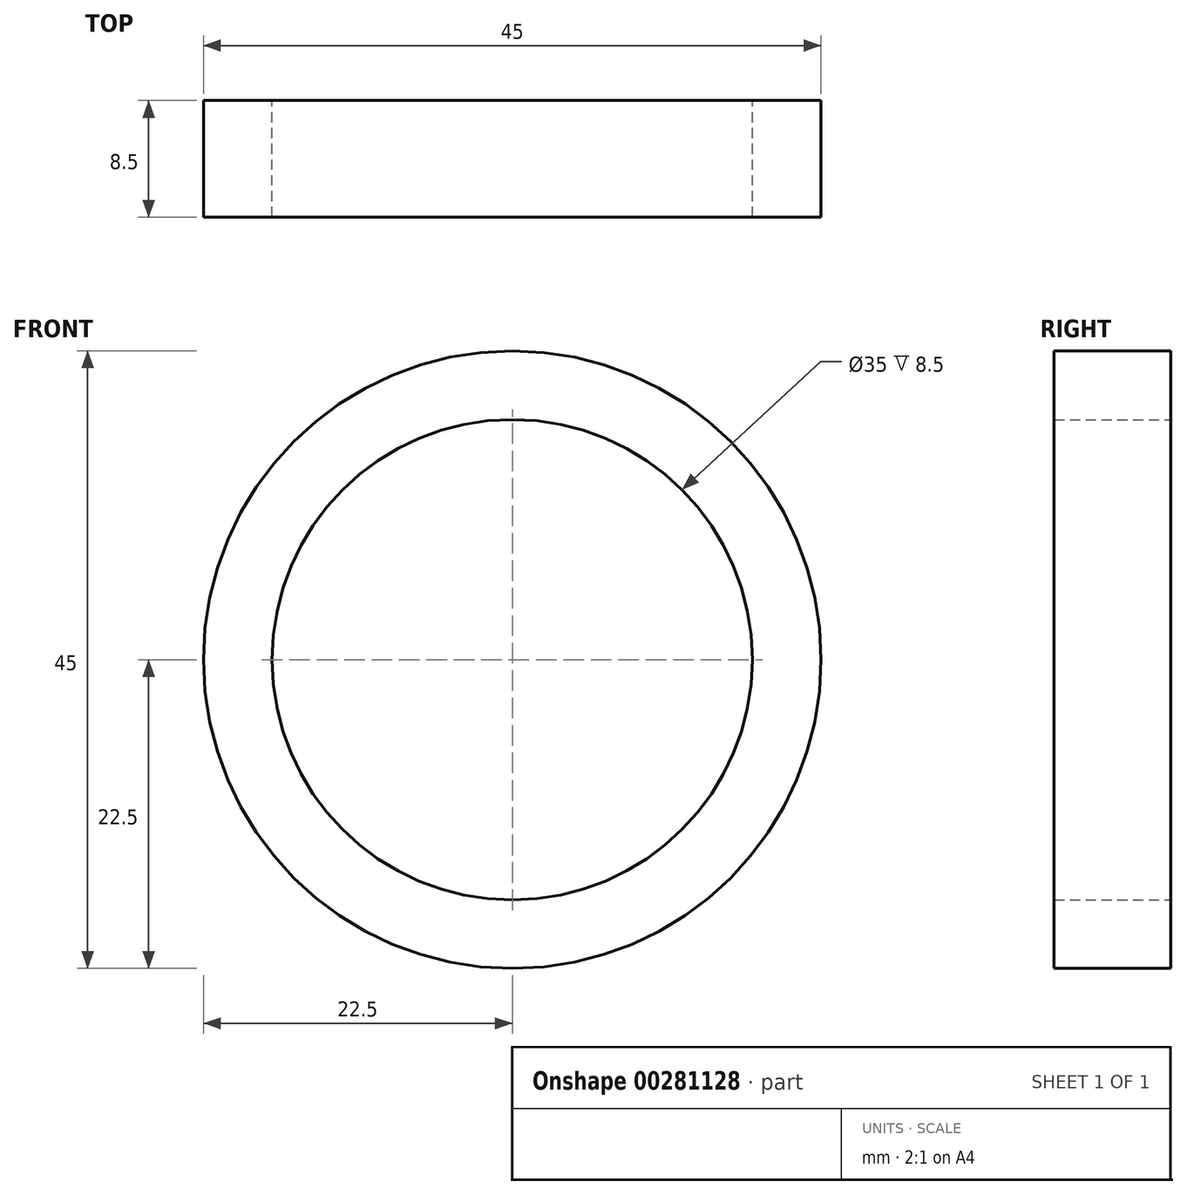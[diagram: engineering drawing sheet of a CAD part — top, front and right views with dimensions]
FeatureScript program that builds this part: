
annotation { "Feature Type Name" : "Feature", "Feature Type Description" : "" }
export const myFeature = defineFeature(function(context is Context, id is Id, definition is map)
    precondition{}
    {
        {
            var Q0;
            Q0=qCreatedBy(makeId("Front.planeOp"),FACE);
            var sketch = newSketch(context, id + "F0", { "sketchPlane" : qUnion([Q0])});
            skCircle(sketch, "E0", {"center": v(0, 0) * mm, "radius": 17.5 * mm});
            skCircle(sketch, "E1", {"center": v(0, 0) * mm, "radius": 22.5 * mm});
            skSolve(sketch);
        }
        {
            var Q0;
            Q0=makeQuery(id+"F0.imprint","IMPRINT",FACE,{"disambiguationData":[TD([[makeQuery(id+"F0.imprint","IMPRINT",EDGE,{"derivedFrom":sQuery(id+"F0.wireOp",EDGE,"E0")}),-1.0]])]});
            extrude(context, id + "F1", {"entities" : qUnion([Q0]), "depth" : 8.5 * mm});
        }
    });
